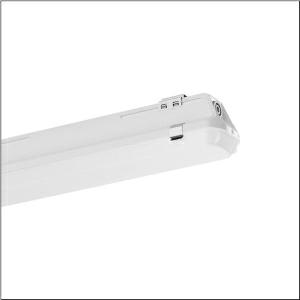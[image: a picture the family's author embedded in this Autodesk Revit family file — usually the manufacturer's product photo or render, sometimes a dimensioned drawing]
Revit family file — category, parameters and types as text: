
# Revit family: monsun_r__11_51fp108p460h_7b9f
name_source: partatom
category: Lighting Fixtures
units: mm (PartAtom-declared; Revit-internal decimal feet)

## family parameters
Cut with Voids When Loaded = No
Host = Face
Light Source = No
Part Type = Normal
Room Calculation Point = No
Round Connector Dimension = Use Diameter
Shared = No

## types (1)
- Monsun® 11 (1 x LED, 6100 lm, 33.9 W, 4000K)
    Apparent Load = 34 VA
    CIE Flux Codes = 47 77 93 94 100
    Color Rendering = 80
    Color Temperature = 4000K
    Default Elevation = 1800 mm
    Description = Monsun® 11, damp-proof luminaire, chain hanger, primary optical cover: enclosure, of PMMA, light emission: direct distribution, primary light characteristic: symmetric, installation type: suspended mounting, surface-mounted, horizontal mounting, vertical mounting, LED, rated luminous flux: 6.100lm, luminous efficacy: 180lm/W, light colour: 840, colour temperature: 4000K, control gear: ECG, with terminal, 3-pole, max. 2.5mm², mains connection: 220..240V, AC, 50/60Hz, rated input power: 34W, luminaire housing, of glass-fibre reinforced polyester, uncoated, bright grey, incl. chain hanger, length: 1.590mm, width: 90mm, height: 88mm, clip for enclosure, of stainless steel (V2A), ceiling mounting element, of stainless steel (V2A), chain hanger, of stainless steel (V2A), protection rating (complete): IP66, insulation class (complete): insulation class I (protective earthing), certification: CE, ENEC, VDE, UKCA, protection symbol: D, impact resistance: IK04, permissible operating ambient temperature: -35..+40°C, standard: EN 50419, EN 60598-2-1, no direct snow, no direct sun, no direct rain, for indoor or canopied outdoor use, corresponds to IFS (International Featured Standards) requirements for safety and quality in the food industry, contact your sales advisor before using the luminaires in applications with unclear chemical exposure, large temperature fluctuations or condensation-forming humidity, LABS conformity tested according to VDMA 24364:2018-05, packaging unit: 1 piece
    Height = 89 mm
    Lamp = 1 x LED
    Lamp Light Flux = 6100 lm
    Lamp Power = 33.9 W
    Lamp count = 1
    Length = 1590 mm
    Luminous efficacy = 180 lm/W
    Manufacturer = Siteco
    ModVariant = No
    Model = 51FP108P460H
    Mounting Place = Ceiling
    Mounting Type = Surface mounted
    Number of Poles = 1
    OnlyDefault = Yes
    Power Factor = 1
    Product Name = Monsun® 11
    Product group = damp-proof luminaire
    ProductGroupID = 301
    Protection Class = Protection class I
    Protection Degree = IP 66
    RLX_Detail_Level = 1
    RLX_Emergency_Light_Flux = 0 lm
    RLX_Emergency_Type = 0
    RLX_Emergency_Type_DB = No
    RlxData = <blob elided: 88213 chars, md5=f1b21601>
    Socket = socket
    Standby Power = 0 W
    System Light Flux = 6100 lm
    System Power = 34 W
    Type Comments = Product without accessories
    Type Image = l_1004748.jpg
    URL = http://relux.com
    VarID = ---
    Voltage = 0 V
    Weight = 0.00 kg
    Width = 90 mm

## geometry (parser evidence)
native form markers: Blend x4, Sweep x12
no freeform markers — native parametric forms only
